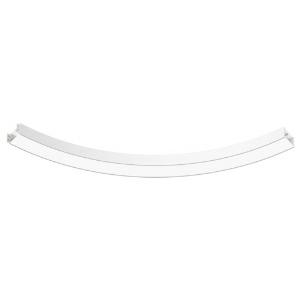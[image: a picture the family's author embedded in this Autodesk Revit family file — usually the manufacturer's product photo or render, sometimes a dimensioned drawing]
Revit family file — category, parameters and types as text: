
# Revit family: super-g_super-g__4000___72deg_hl_dir_indirekt_led__55_2w_8520lm_3000k_cri_80_430-1500_4130
name_source: partatom
category: Leuchten
revit_build: Autodesk Revit 2016 (Build: 20190508_0715(x64)
units: mm (PartAtom-declared; Revit-internal decimal feet)

## family parameters
Basisbauteil = Fläche
Beim Laden mit Abzugskörper schneiden = Nein
Bemaßung runder Anschluss = Durchmesser verwenden
Gemeinsam genutzt = Nein
Lichtquelle = Nein
Raumberechnungspunkt = Nein
Teiletyp = Normal

## types (1)
- 430-1500- (1 x LED, 1065 lm, 3000K)
    Approval mark = CE
    Beschreibung = The insert consists of aluminum-extruded profile. Charming SOFT-EDGE design ensure unparalleled styling. The ballast is integrated and allows for an operation with 220-240V (50/60Hz). SUPER-G (# 430-1500) ist not dimmable (on/off).
    CIE Flux Codes = 48 80 96 61 70
    Color Rendering = 1B/80…89
    Color Temperature = 3000K
    Height = 120 mm
    Hersteller = Prolicht
    Lamp Light Flux = 1065 lm
    Lamp count = 1
    Lampe = 1 x LED
    Length = 314 mm
    Luminous efficacy = 98 lm/W
    ModVariant = Nein
    Modell = 430-1500
    Mounting Place = Ceiling
    Mounting Type = Pendant
    Number of Poles = 1
    OnlyDefault = Ja
    Power Factor = 1
    Product Name = SUPER-G__SUPER-G  4000 / 72° HL dir/indirekt LED: 55,2W 8520lm 3000K CRI:80
    Product group = Suspended profile systems
    ProductGroupID = 944
    Protection Class = Protection class I
    Protection Degree = IP 20
    RLX_Detail_Level = 1
    RlxData = <blob elided: 35797 chars, md5=177455d8>
    Scheinlast = 61 VA
    Socket = socket
    Standby Power = 0 W
    System Light Flux = 5948 lm
    System Power = 61 W
    Typenbild = 430-1500.jpg
    URL = http://relux.com
    VarID = 430-1500-
    Voltage = 0 V
    Vorgabe-Ansicht = 1800 mm
    Weight = 0.00 kg
    Width = 150 mm

## geometry (parser evidence)
native form markers: Sweep x50
no freeform markers — native parametric forms only
